# Revit family: Sanitary_Toilet-Seats_hansgrohe_22401007-Lavapura-Uno-Shower-toilet-B-40_1
name_source: partatom
category: Specialty Equipment
revit_build: Autodesk Revit 2015 (Build: 20140903_1530(x64)
units: mm (PartAtom-declared; Revit-internal decimal feet)

## types (1)
- White
    BIMobject category = Toilet Seats
    BIMobject category code = sanitary-toilet-seats
    BIMobject main category = Sanitary
    BIMobject main category code = sanitary
    Brand url = http://www.hansgrohe-int.com
    Default Elevation = 1219.2 mm  [stored 4 ft]
    Design country = Germany
    Edition number = 1
    GTIN code = https://4059625263907
    IFC Classification = Sanitary Terminal
    Installation instructions = https://www.hansgrohe.com.cn
    Manufacturer country = Germany
    Manufacturer name = hansgrohe
    Material main = Vitreous china
    Product Guid = d537cccb-b481-48d8-af1c-f4ca03dc716b
    Product SKU = 22401007
    Product data url = https://bimobject.com
    Product family = Shower toilet
    Product group = Lavapura
    Product name = 22401007 Lavapura Uno Shower toilet B 400
    Product url = https://www.hansgrohe.com.cn
    QR code = http://bimobject.com
    Technical description = https://www.hansgrohe.com.cn

note: [stored X ft] marks values corroborated as IEEE doubles in the binary element streams (Revit-internal decimal feet)

## geometry (parser evidence)
native form markers: Sweep x2
no freeform markers — native parametric forms only
